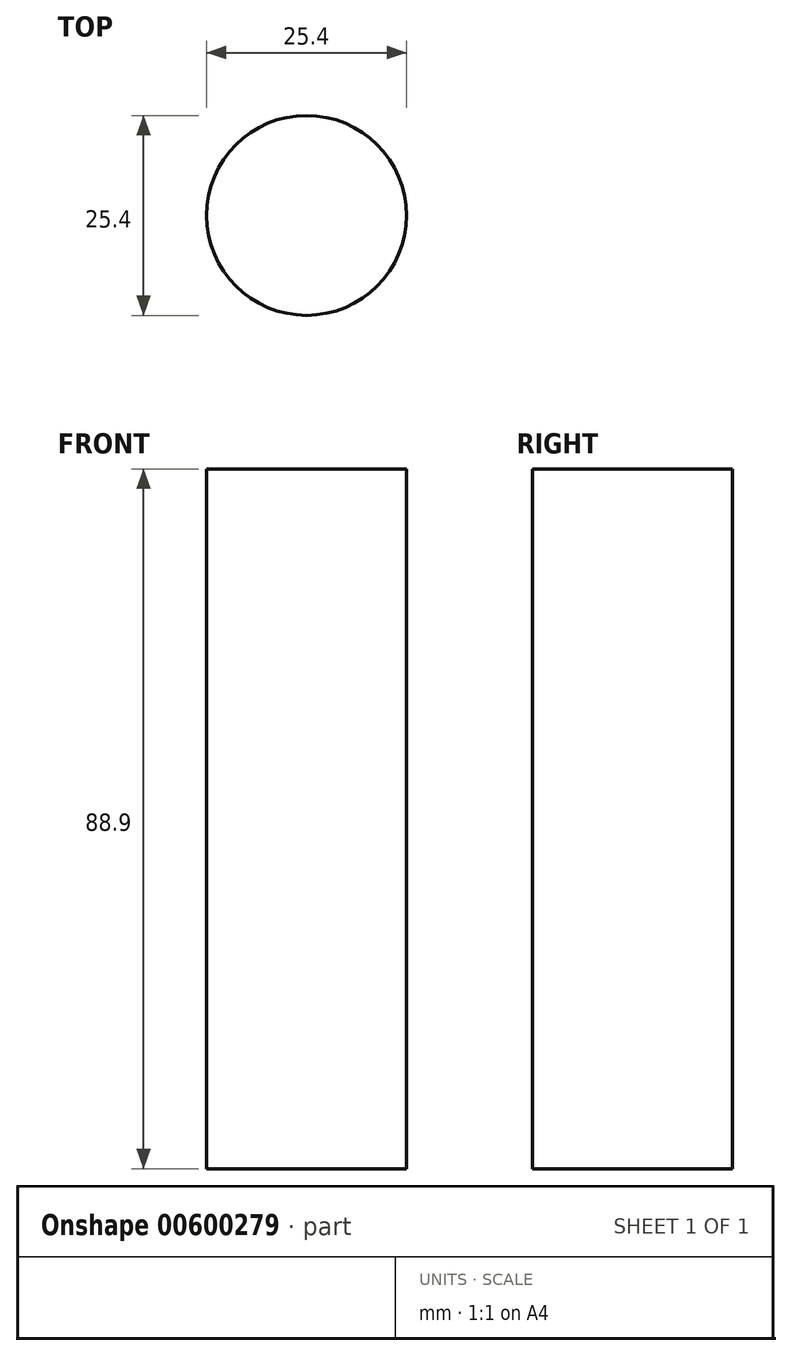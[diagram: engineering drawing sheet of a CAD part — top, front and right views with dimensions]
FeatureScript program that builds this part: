
annotation { "Feature Type Name" : "Feature", "Feature Type Description" : "" }
export const myFeature = defineFeature(function(context is Context, id is Id, definition is map)
    precondition{}
    {
        {
            var Q0;
            Q0=qCreatedBy(makeId("Top.planeOp"),FACE);
            var sketch = newSketch(context, id + "F0", { "sketchPlane" : qUnion([Q0])});
            skCircle(sketch, "E0", {"center": v(0, 0) * mm, "radius": 12.7 * mm});
            skSolve(sketch);
        }
        {
            var Q0;
            Q0 = qSketchRegion(id + "F0", true);
            extrude(context, id + "F1", {"entities" : qUnion([Q0]), "depth" : 88.9 * mm, "offsetDistance" : 25.4 * mm});
        }
    });
